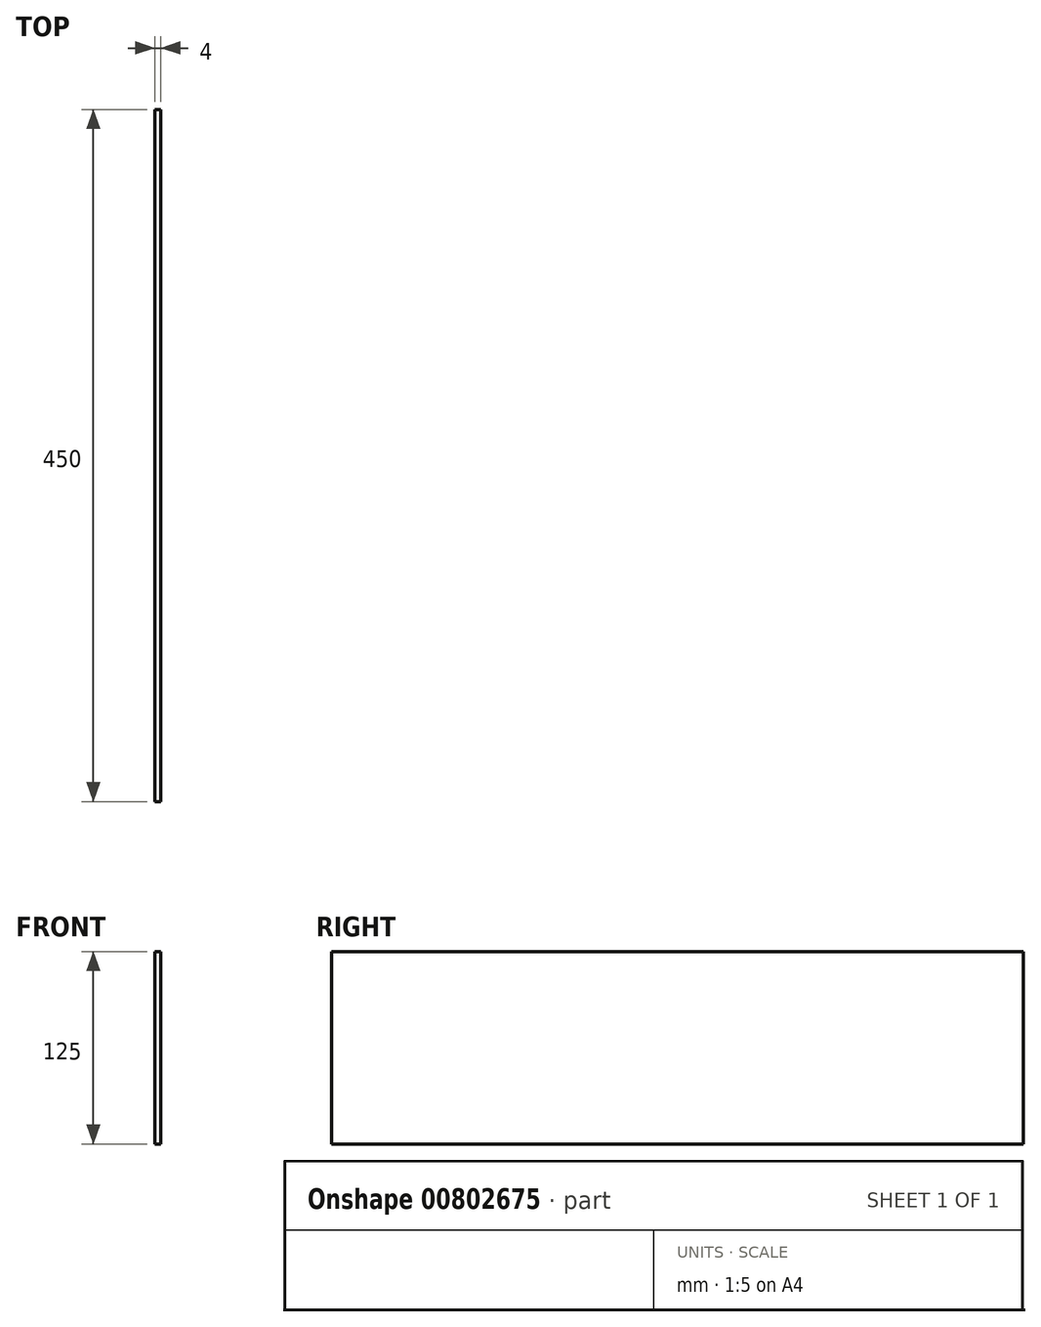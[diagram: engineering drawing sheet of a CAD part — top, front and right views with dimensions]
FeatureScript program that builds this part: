
annotation { "Feature Type Name" : "Feature", "Feature Type Description" : "" }
export const myFeature = defineFeature(function(context is Context, id is Id, definition is map)
    precondition{}
    {
        {
            var Q0;
            Q0=qCreatedBy(makeId("Right.planeOp"),FACE);
            var sketch = newSketch(context, id + "F0", { "sketchPlane" : qUnion([Q0])});
            skLineSegment(sketch, "E0.bottom", {"start": v(0, 0) * mm, "end": v(450, 0) * mm});
            skLineSegment(sketch, "E0.top", {"start": v(0, 125) * mm, "end": v(450, 125) * mm});
            skLineSegment(sketch, "E0.left", {"start": v(0, 0) * mm, "end": v(0, 125) * mm});
            skLineSegment(sketch, "E0.right", {"start": v(450, 0) * mm, "end": v(450, 125) * mm});
            skSolve(sketch);
        }
        {
            var Q0;
            Q0=makeQuery(id+"F0.imprint","IMPRINT",FACE,{"disambiguationData":[TD([[makeQuery(id+"F0.imprint","IMPRINT",EDGE,{"derivedFrom":sQuery(id+"F0.wireOp",EDGE,"E0.bottom")}),1.0]])]});
            extrude(context, id + "F1", {"entities" : qUnion([Q0]), "depth" : 4 * mm, "offsetDistance" : 25 * mm});
        }
    });
